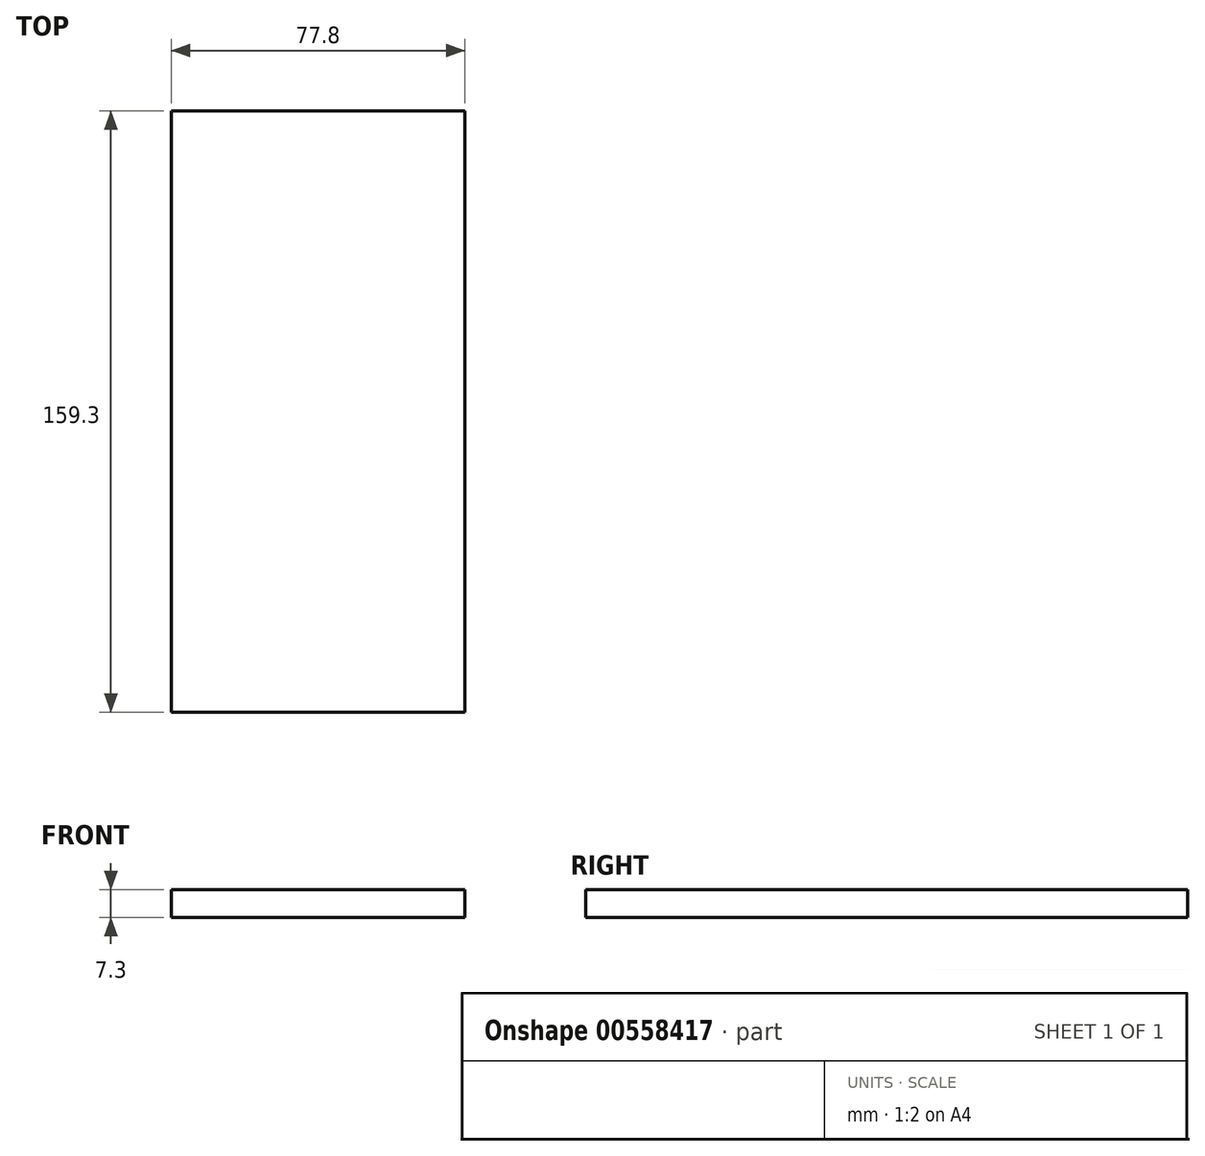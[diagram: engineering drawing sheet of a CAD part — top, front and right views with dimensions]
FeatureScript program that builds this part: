
annotation { "Feature Type Name" : "Feature", "Feature Type Description" : "" }
export const myFeature = defineFeature(function(context is Context, id is Id, definition is map)
    precondition{}
    {
        {
            var Q0;
            Q0=qCreatedBy(makeId("Top.planeOp"),FACE);
            var sketch = newSketch(context, id + "F0", { "sketchPlane" : qUnion([Q0])});
            skLineSegment(sketch, "E0.bottom", {"start": v(-76.92, -69.65) * mm, "end": v(0.88, -69.65) * mm});
            skLineSegment(sketch, "E0.top", {"start": v(-76.92, 89.65) * mm, "end": v(0.88, 89.65) * mm});
            skLineSegment(sketch, "E0.left", {"start": v(-76.92, -69.65) * mm, "end": v(-76.92, 89.65) * mm});
            skLineSegment(sketch, "E0.right", {"start": v(0.88, -69.65) * mm, "end": v(0.88, 89.65) * mm});
            skSolve(sketch);
        }
        {
            var Q0;
            Q0 = qSketchRegion(id + "F0", true);
            extrude(context, id + "F1", {"entities" : qUnion([Q0]), "depth" : 7.3 * mm, "offsetDistance" : 25 * mm});
        }
    });
